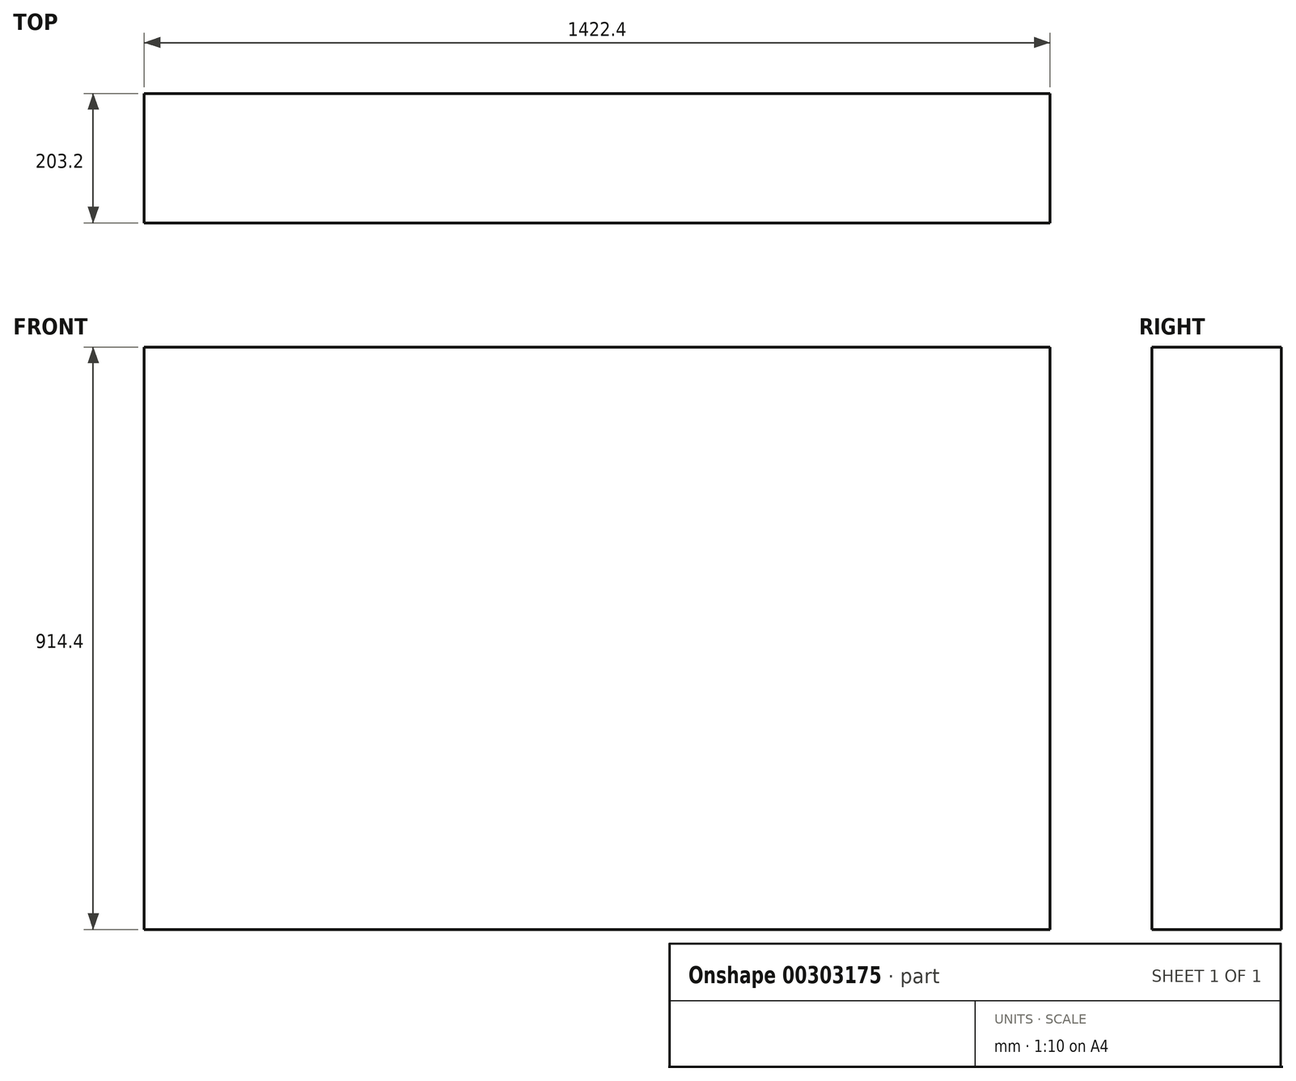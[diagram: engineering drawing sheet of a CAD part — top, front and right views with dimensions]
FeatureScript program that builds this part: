
annotation { "Feature Type Name" : "Feature", "Feature Type Description" : "" }
export const myFeature = defineFeature(function(context is Context, id is Id, definition is map)
    precondition{}
    {
        {
            var Q0;
            Q0=qCreatedBy(makeId("Top.planeOp"),FACE);
            var sketch = newSketch(context, id + "F1", { "sketchPlane" : qUnion([Q0])});
            skLineSegment(sketch, "E0.bottom", {"start": v(711.2, 101.6) * mm, "end": v(-711.2, 101.6) * mm});
            skLineSegment(sketch, "E0.top", {"start": v(711.2, -101.6) * mm, "end": v(-711.2, -101.6) * mm});
            skLineSegment(sketch, "E0.left", {"start": v(711.2, 101.6) * mm, "end": v(711.2, -101.6) * mm});
            skLineSegment(sketch, "E0.right", {"start": v(-711.2, 101.6) * mm, "end": v(-711.2, -101.6) * mm});
            skPoint(sketch, "E0.middle", {"position": v(0, 0) * mm});
            skSolve(sketch);
        }
        {
            var Q0;
            Q0=makeQuery(id+"F1.imprint","IMPRINT",FACE,{"disambiguationData":[TD([[makeQuery(id+"F1.imprint","IMPRINT",EDGE,{"derivedFrom":sQuery(id+"F1.wireOp",EDGE,"E0.bottom")}),1.0]])]});
            extrude(context, id + "F0", {"entities" : qUnion([Q0]), "depth" : 914.4 * mm});
        }
    });
